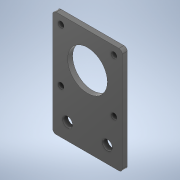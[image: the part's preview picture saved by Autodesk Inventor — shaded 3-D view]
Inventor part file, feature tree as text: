
AUTODESK INVENTOR PART (.ipt)
format: ipt  version: 2020 (Build 240168000, 168)  size: 150,528 bytes
history: native  units: mm
features: extrude x1, fillet x1, sketch x1
ambient origin geometry x8: Origin, YZ Plane, XZ Plane, XY Plane, X Axis, Y Axis, Z Axis, Center Point
bodies: Solid1 (feature_tree)
feature tree (3):
  extrude  "Extrusion1"  Depth=64.0mm
  fillet  "Fillet1"  Radius=43.0mm
  sketch  "Sketch1"  dims[d0=42.0mm d1=64.0mm d2=43.0mm d3=21.0mm d4=24.0mm d5=6.0mm d6=6.0mm d7=10.0mm d8=10.0mm d9=12.0mm d10=12.0mm d11=32.0mm d12=32.0mm d13=3.5mm d14=3.5mm d15=3.5mm d16=3.5mm d17=3.0mm d18=0.0mm d19=2.0mm]
